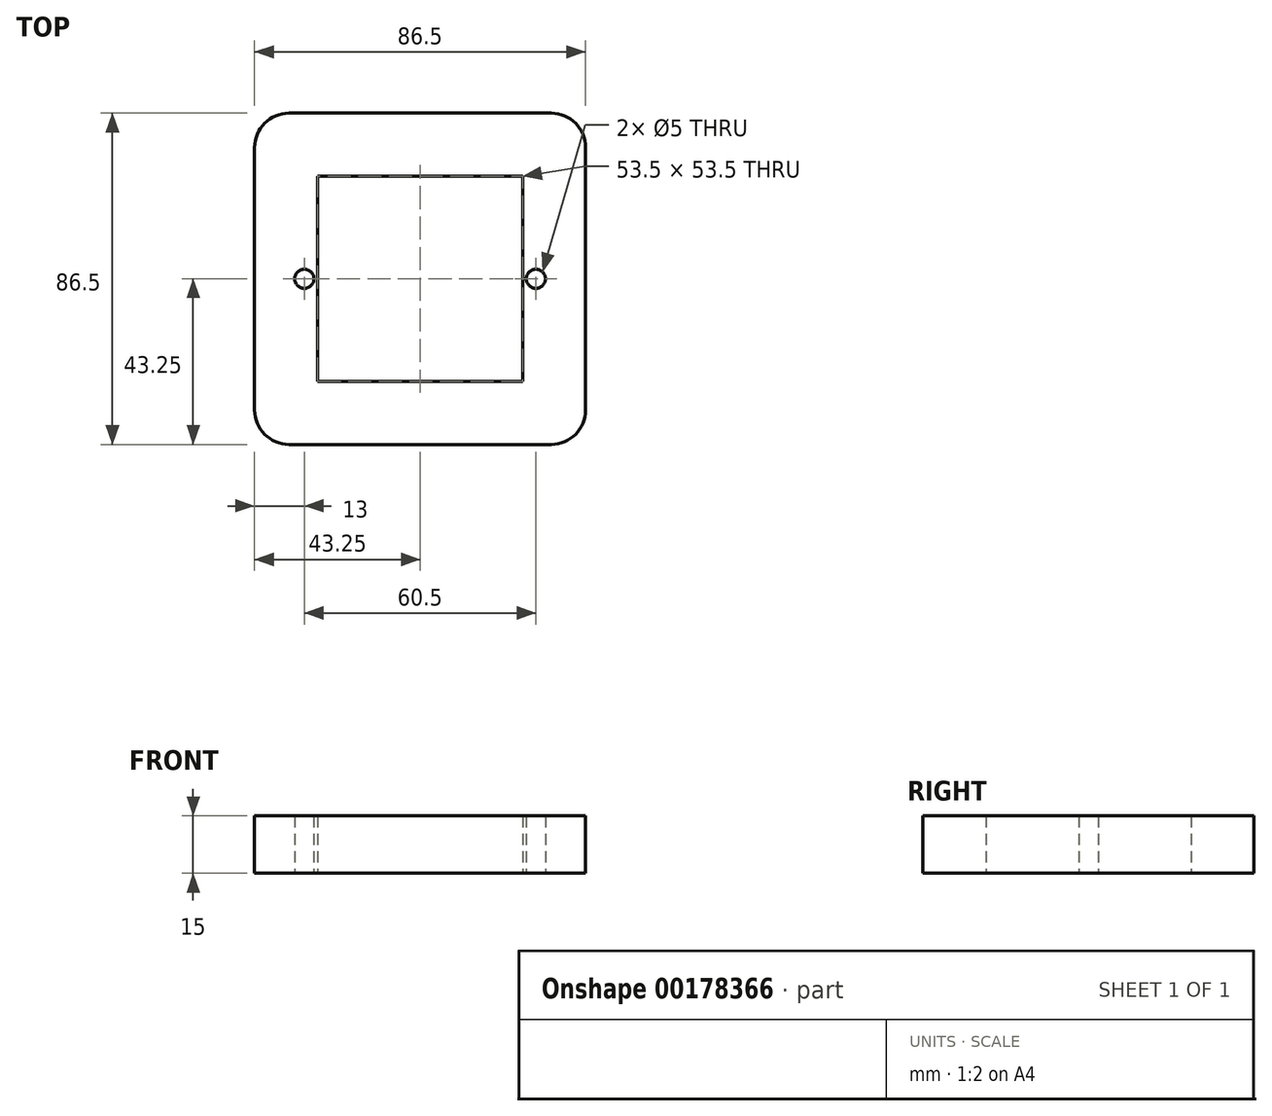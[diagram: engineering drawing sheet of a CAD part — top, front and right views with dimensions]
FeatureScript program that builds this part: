
annotation { "Feature Type Name" : "Feature", "Feature Type Description" : "" }
export const myFeature = defineFeature(function(context is Context, id is Id, definition is map)
    precondition{}
    {
        {
            var Q0;
            Q0=qCreatedBy(makeId("Top.planeOp"),FACE);
            var sketch = newSketch(context, id + "F0", { "sketchPlane" : qUnion([Q0])});
            skLineSegment(sketch, "E0.bottom", {"start": v(34.25, -43.25) * mm, "end": v(-34.25, -43.25) * mm});
            skLineSegment(sketch, "E0.top", {"start": v(34.25, 43.25) * mm, "end": v(-34.25, 43.25) * mm});
            skLineSegment(sketch, "E0.left", {"start": v(43.25, -34.25) * mm, "end": v(43.25, 34.25) * mm});
            skLineSegment(sketch, "E0.right", {"start": v(-43.25, -34.25) * mm, "end": v(-43.25, 34.25) * mm});
            skPoint(sketch, "E0.middle", {"position": v(0, 0) * mm});
            skLineSegment(sketch, "E1.0", {"start": v(26.75, -26.75) * mm, "end": v(26.75, 26.75) * mm});
            skLineSegment(sketch, "E1.1", {"start": v(26.75, -26.75) * mm, "end": v(-26.75, -26.75) * mm});
            skLineSegment(sketch, "E1.2", {"start": v(-26.75, -26.75) * mm, "end": v(-26.75, 26.75) * mm});
            skLineSegment(sketch, "E1.3", {"start": v(26.75, 26.75) * mm, "end": v(-26.75, 26.75) * mm});
            skPoint(sketch, "E2.visualSharp", {"position": v(-43.25, 43.25) * mm});
            skArc(sketch, "E2.filletArc", {"start": v(-34.25, 43.25) * mm, "mid": v(-40.61, 40.61) * mm, "end": v(-43.25, 34.25) * mm});
            skPoint(sketch, "E3.visualSharp", {"position": v(43.25, 43.25) * mm});
            skArc(sketch, "E3.filletArc", {"start": v(43.25, 34.25) * mm, "mid": v(40.61, 40.61) * mm, "end": v(34.25, 43.25) * mm});
            skPoint(sketch, "E4.visualSharp", {"position": v(43.25, -43.25) * mm});
            skArc(sketch, "E4.filletArc", {"start": v(34.25, -43.25) * mm, "mid": v(40.61, -40.61) * mm, "end": v(43.25, -34.25) * mm});
            skPoint(sketch, "E5.visualSharp", {"position": v(-43.25, -43.25) * mm});
            skArc(sketch, "E5.filletArc", {"start": v(-43.25, -34.25) * mm, "mid": v(-40.61, -40.61) * mm, "end": v(-34.25, -43.25) * mm});
            skCircle(sketch, "E6", {"center": v(-30.25, 0) * mm, "radius": 2.5 * mm});
            skCircle(sketch, "E7", {"center": v(30.25, 0) * mm, "radius": 2.5 * mm});
            skSolve(sketch);
        }
        {
            var Q0;
            Q0=makeQuery(id+"F0.imprint","IMPRINT",FACE,{"disambiguationData":[TD([[makeQuery(id+"F0.imprint","IMPRINT",EDGE,{"derivedFrom":sQuery(id+"F0.wireOp",EDGE,"E0.bottom")}),-1.0]])]});
            extrude(context, id + "F1", {"entities" : qUnion([Q0]), "depth" : 15 * mm});
        }
    });
